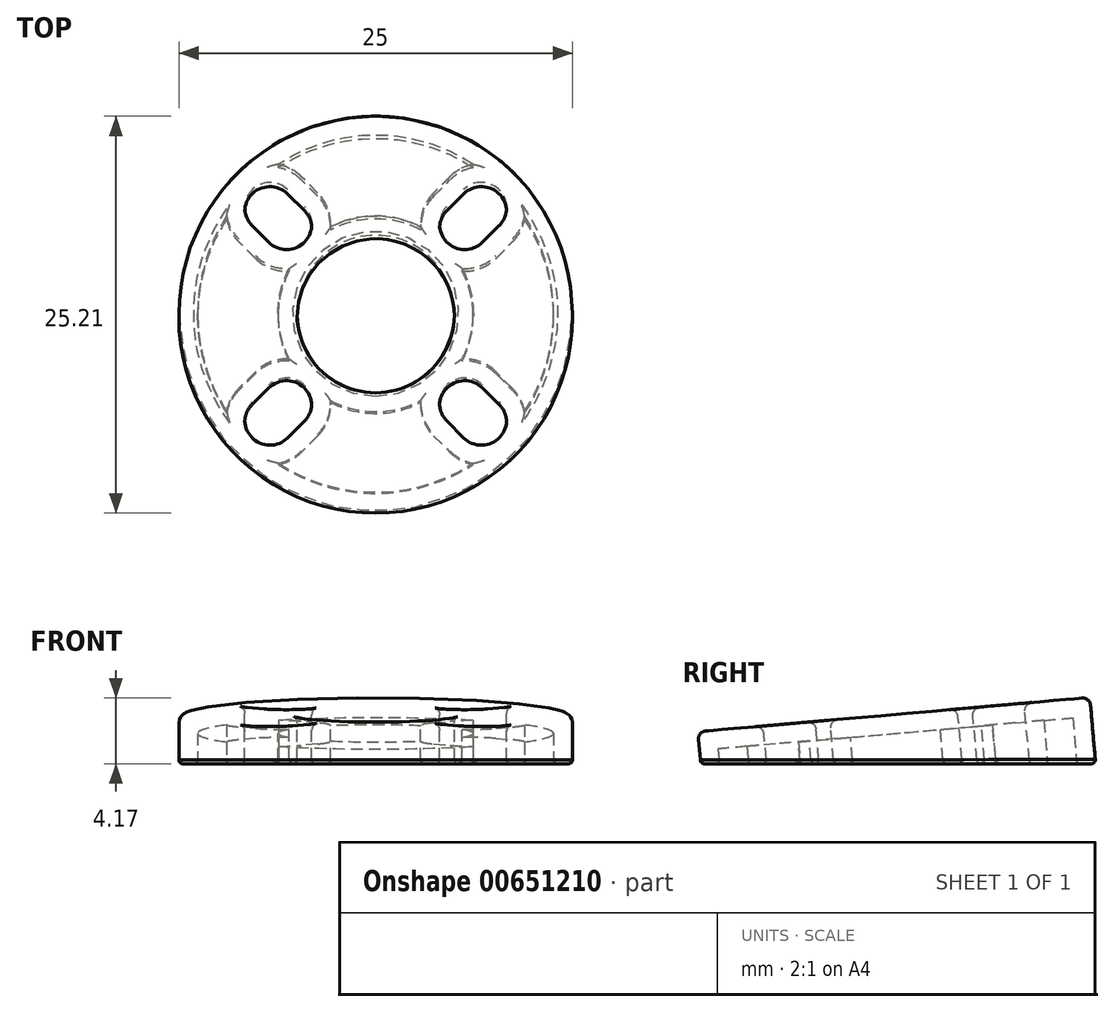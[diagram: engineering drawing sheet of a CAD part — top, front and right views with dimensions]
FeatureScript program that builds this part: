
annotation { "Feature Type Name" : "Feature", "Feature Type Description" : "" }
export const myFeature = defineFeature(function(context is Context, id is Id, definition is map)
    precondition{}
    {
        {
            var Q0;
            Q0=qCreatedBy(makeId("Front.planeOp"),FACE);
            var sketch = newSketch(context, id + "F0", { "sketchPlane" : qUnion([Q0])});
            skLineSegment(sketch, "E0", {"start": v(0, 35.33) * mm, "end": v(0, -43) * mm, "construction": true});
            skSolve(sketch);
        }
        {
            var Q0;
            Q0=qCreatedBy(makeId("Top.planeOp"),FACE);
            var sketch = newSketch(context, id + "F1", { "sketchPlane" : qUnion([Q0])});
            skCircle(sketch, "E1", {"center": v(0, 0) * mm, "radius": 12.5 * mm});
            skSolve(sketch);
        }
        {
            var Q0;
            Q0=qCreatedBy(makeId("Top.planeOp"),FACE);
            var sketch = newSketch(context, id + "F2", { "sketchPlane" : qUnion([Q0])});
            skArc(sketch, "E2", {"start": v(8, 1.6) * mm, "mid": v(6.4, 0) * mm, "end": v(8, -1.6) * mm});
            skArc(sketch, "E3", {"start": v(9.5, -1.6) * mm, "mid": v(11.1, 0) * mm, "end": v(9.5, 1.6) * mm});
            skLineSegment(sketch, "E4", {"start": v(6.4, -1.6) * mm, "end": v(8, -1.6) * mm, "construction": true});
            skLineSegment(sketch, "E5", {"start": v(6.18, 1.6) * mm, "end": v(7.78, 1.6) * mm, "construction": true});
            skLineSegment(sketch, "E6", {"start": v(7.78, 1.6) * mm, "end": v(12.2, 1.6) * mm, "construction": true});
            skLineSegment(sketch, "E7", {"start": v(6.98, 1.6) * mm, "end": v(11.18, 1.6) * mm});
            skLineSegment(sketch, "E8", {"start": v(6.85, -1.6) * mm, "end": v(10.81, -1.6) * mm});
            skLineSegment(sketch, "E9.trimOffspring", {"start": v(9.5, -1.6) * mm, "end": v(11.38, -1.6) * mm, "construction": true});
            skLineSegment(sketch, "E10.1.0", {"start": v(1.6, 6.85) * mm, "end": v(1.6, 10.81) * mm});
            skLineSegment(sketch, "E10.1.1", {"start": v(1.6, 9.5) * mm, "end": v(1.6, 11.38) * mm, "construction": true});
            skLineSegment(sketch, "E10.1.2", {"start": v(-1.6, 7.78) * mm, "end": v(-1.6, 12.2) * mm, "construction": true});
            skLineSegment(sketch, "E10.1.3", {"start": v(1.6, 6.4) * mm, "end": v(1.6, 8) * mm, "construction": true});
            skArc(sketch, "E10.1.4", {"start": v(1.6, 9.5) * mm, "mid": v(0, 11.1) * mm, "end": v(-1.6, 9.5) * mm});
            skArc(sketch, "E10.1.5", {"start": v(-1.6, 8) * mm, "mid": v(0, 6.4) * mm, "end": v(1.6, 8) * mm});
            skLineSegment(sketch, "E10.1.6", {"start": v(-1.6, 6.98) * mm, "end": v(-1.6, 11.18) * mm});
            skLineSegment(sketch, "E10.1.7", {"start": v(-1.6, 6.18) * mm, "end": v(-1.6, 7.78) * mm, "construction": true});
            skLineSegment(sketch, "E10.2.0", {"start": v(-6.85, 1.6) * mm, "end": v(-10.81, 1.6) * mm});
            skLineSegment(sketch, "E10.2.1", {"start": v(-9.5, 1.6) * mm, "end": v(-11.38, 1.6) * mm, "construction": true});
            skLineSegment(sketch, "E10.2.2", {"start": v(-7.78, -1.6) * mm, "end": v(-12.2, -1.6) * mm, "construction": true});
            skLineSegment(sketch, "E10.2.3", {"start": v(-6.4, 1.6) * mm, "end": v(-8, 1.6) * mm, "construction": true});
            skArc(sketch, "E10.2.4", {"start": v(-9.5, 1.6) * mm, "mid": v(-11.1, 0) * mm, "end": v(-9.5, -1.6) * mm});
            skArc(sketch, "E10.2.5", {"start": v(-8, -1.6) * mm, "mid": v(-6.4, 0) * mm, "end": v(-8, 1.6) * mm});
            skLineSegment(sketch, "E10.2.6", {"start": v(-6.98, -1.6) * mm, "end": v(-11.18, -1.6) * mm});
            skLineSegment(sketch, "E10.2.7", {"start": v(-6.18, -1.6) * mm, "end": v(-7.78, -1.6) * mm, "construction": true});
            skLineSegment(sketch, "E10.3.0", {"start": v(-1.6, -6.85) * mm, "end": v(-1.6, -10.81) * mm});
            skLineSegment(sketch, "E10.3.1", {"start": v(-1.6, -9.5) * mm, "end": v(-1.6, -11.38) * mm, "construction": true});
            skLineSegment(sketch, "E10.3.2", {"start": v(1.6, -7.78) * mm, "end": v(1.6, -12.2) * mm, "construction": true});
            skLineSegment(sketch, "E10.3.3", {"start": v(-1.6, -6.4) * mm, "end": v(-1.6, -8) * mm, "construction": true});
            skArc(sketch, "E10.3.4", {"start": v(-1.6, -9.5) * mm, "mid": v(0, -11.1) * mm, "end": v(1.6, -9.5) * mm});
            skArc(sketch, "E10.3.5", {"start": v(1.6, -8) * mm, "mid": v(0, -6.4) * mm, "end": v(-1.6, -8) * mm});
            skLineSegment(sketch, "E10.3.6", {"start": v(1.6, -6.98) * mm, "end": v(1.6, -11.18) * mm});
            skLineSegment(sketch, "E10.3.7", {"start": v(1.6, -6.18) * mm, "end": v(1.6, -7.78) * mm, "construction": true});
            skPoint(sketch, "E10.center", {"position": v(0, 0) * mm});
            skCircle(sketch, "E11", {"center": v(0, 0) * mm, "radius": 5 * mm});
            skSolve(sketch);
        }
        {
            var Q0;
            Q0 = qSketchRegion(id + "F1", true);
            extrude(context, id + "F3", {"entities" : qUnion([Q0]), "depth" : 5 * mm, "offsetDistance" : 25 * mm});
        }
        {
            var Q0;
            Q0 = qSketchRegion(id + "F2", true);
            extrude(context, id + "F4", {"entities" : qUnion([Q0]), "operationType" : NewBodyOperationType.REMOVE, "endBound" : BoundingType.SYMMETRIC, "oppositeDirection" : true, "depth" : 25 * mm, "offsetDistance" : 25 * mm});
        }
        {
            var Q0;
            Q0=makeQuery(id+"F3.opExtrude","SWEPT_BODY",BODY,{"disambiguationData":[OSD([sQuery(id+"F1.wireOp",EDGE,"E1")])]});
            var Q1;
            Q1=sQuery(id+"F0.wireOp",EDGE,"E0");
            transform(context, id + "F5", {"entities" : qUnion([Q0]), "transformType" : TransformType.ROTATION, "transformAxis" : qUnion([Q1]), "angle" : 45 * degree, "makeCopy" : false});
        }
        {
            var Q0;
            Q0=makeQuery(id+"F3.opExtrude","CAP_FACE",FACE,{"disambiguationData":[OSD([sQuery(id+"F1.wireOp",EDGE,"E1")])],"isStart":true});
            cPlane(context, id + "F6", {"entities" : qUnion([Q0]), "cplaneType" : CPlaneType.OFFSET, "offset" : 5 * mm, "width" : 150 * mm, "height" : 150 * mm});
        }
        {
            var Q0;
            Q0=makeQuery(id+"F3.opExtrude","SWEPT_BODY",BODY,{"disambiguationData":[OSD([sQuery(id+"F1.wireOp",EDGE,"E1")])]});
            var Q1;
            Q1=sQuery(id+"F2.wireOp",EDGE,"E8");
            transform(context, id + "F7", {"entities" : qUnion([Q0]), "transformType" : TransformType.ROTATION, "transformAxis" : qUnion([Q1]), "angle" : 5 * degree, "makeCopy" : false});
        }
        {
            var Q0;
            Q0=qCreatedBy(id+"F6.planeOp",FACE);
            var sketch = newSketch(context, id + "F8", { "sketchPlane" : qUnion([Q0])});
            skLineSegment(sketch, "E12.bottom", {"start": v(-18.67, -18.95) * mm, "end": v(23.1, -18.95) * mm});
            skLineSegment(sketch, "E12.top", {"start": v(-18.67, 22.81) * mm, "end": v(23.1, 22.81) * mm});
            skLineSegment(sketch, "E12.left", {"start": v(-18.67, -18.95) * mm, "end": v(-18.67, 22.81) * mm});
            skLineSegment(sketch, "E12.right", {"start": v(23.1, -18.95) * mm, "end": v(23.1, 22.81) * mm});
            skSolve(sketch);
        }
        {
            var Q0;
            Q0 = qSketchRegion(id + "F8", true);
            extrude(context, id + "F9", {"entities" : qUnion([Q0]), "operationType" : NewBodyOperationType.REMOVE, "oppositeDirection" : true, "depth" : 7 * mm, "offsetDistance" : 25 * mm});
        }
        {
            var Q0;
            Q0=makeQuery(id+"F9.boolean.opBoolean","COPY",FACE,{"derivedFrom":makeQuery(id+"F9.opExtrude","CAP_FACE",FACE,{"disambiguationData":[OSD([sQuery(id+"F8.wireOp",EDGE,"E12.bottom"),sQuery(id+"F8.wireOp",EDGE,"E12.top"),sQuery(id+"F8.wireOp",EDGE,"E12.left"),sQuery(id+"F8.wireOp",EDGE,"E12.right")])],"isStart":false})});
            shell(context, id + "F10", {"entities" : qUnion([Q0]), "thickness" : 1.2 * mm});
        }
        {
            var Q0;
            Q0=makeQuery(id+"F9.boolean.opBoolean","COPY",FACE,{"derivedFrom":makeQuery(id+"F9.opExtrude","CAP_FACE",FACE,{"disambiguationData":[OSD([sQuery(id+"F8.wireOp",EDGE,"E12.bottom"),sQuery(id+"F8.wireOp",EDGE,"E12.top"),sQuery(id+"F8.wireOp",EDGE,"E12.left"),sQuery(id+"F8.wireOp",EDGE,"E12.right")])],"isStart":false})});
            fillet(context, id + "F11", {"entities" : qUnion([Q0]), "radius" : 0.25 * mm, "tangentPropagation" : true, "allowEdgeOverflow" : false});
        }
        {
            var Q0;
            Q0=makeQuery(id+"F3.opExtrude","CAP_FACE",FACE,{"disambiguationData":[OSD([sQuery(id+"F1.wireOp",EDGE,"E1")])],"isStart":false});
            fillet(context, id + "F12", {"entities" : qUnion([Q0]), "radius" : 0.5 * mm, "tangentPropagation" : true, "allowEdgeOverflow" : false});
        }
    });
